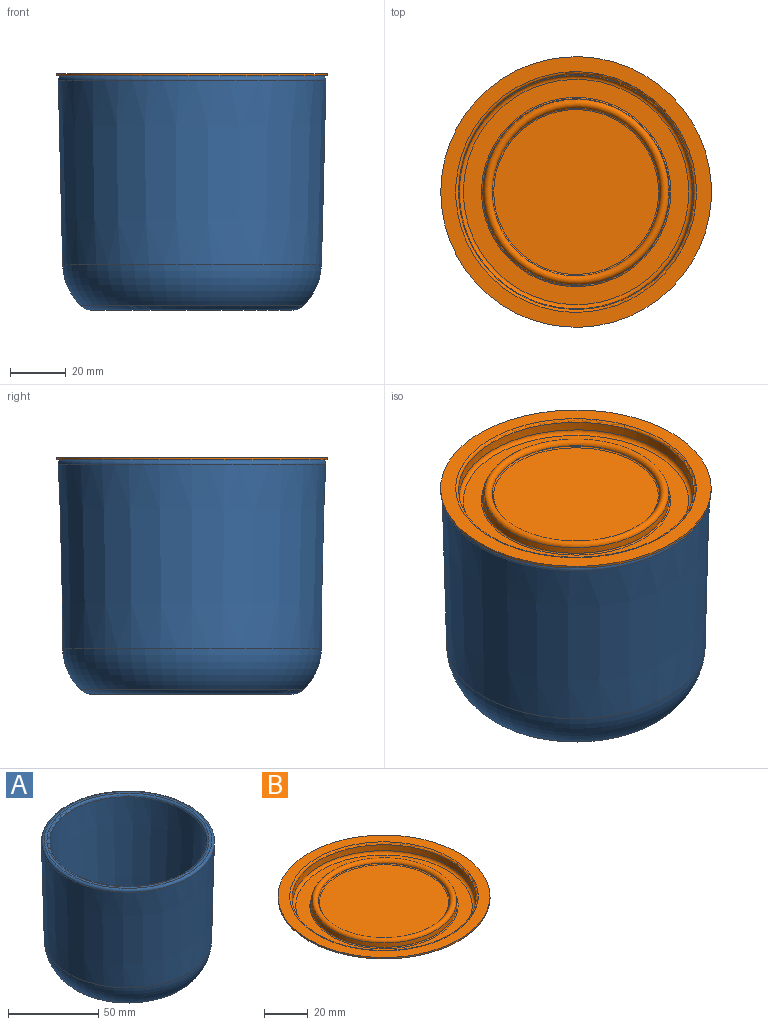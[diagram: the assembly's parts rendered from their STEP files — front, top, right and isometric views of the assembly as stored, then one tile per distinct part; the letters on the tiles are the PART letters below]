
ASSEMBLY  parts=2 mates=1
PART A: 11 faces, bbox 103.8x103.8x88.2 mm
  f0: cone r=43.5mm half-angle=3.5deg, axis (0,0,1), area 18136.1mm2, adj f3,f6
  f1: torus R=35.76mm, axis (0,0,1), area 1107.2mm2, adj f8,f10
  f2: plane 72.35x72.35mm, normal (0,0,1), area 4111.6mm2, adj f3
  f3: torus R=36.18mm, axis (0,0,-1), area 1082.9mm2, adj f0,f2
  f4: torus R=46.46mm, axis (0,0,-1), area 712.8mm2, adj f5,f7
  f5: plane 92.93x92.93mm, normal (0,0,1), area 445.6mm2, adj f4,f6
  f6: torus R=44.91mm, axis (0,0,-1), area 625.9mm2, adj f0,f5
  f7: cone r=46mm half-angle=1.4deg, axis (0,0,1), area 19603.5mm2, adj f4,f9
  f8: cone r=38.2mm half-angle=45.7deg, axis (0,0,1), area 42.3mm2, adj f1,f9
  f9: torus R=25.4mm, axis (0,0,-1), area 4507.6mm2, adj f7,f8
  f10: sphere r=426.91mm, area 4023.6mm2, adj f1
PART B: 23 faces, bbox 97x97x6 mm
  f0: plane 59.27x59.27mm, normal (0,0,-1), area 2758.8mm2, adj f18
  f1: cone r=30.55mm half-angle=5deg, axis (0,0,1), area 33.7mm2, adj f2,f18
  f2: torus R=31.64mm, axis (0,0,-1), area 589.9mm2, adj f1,f3
  f3: cone r=32.64mm half-angle=5deg, axis (0,0,-1), area 490.3mm2, adj f2,f17
  f4: plane 80.92x80.92mm, normal (0,0,-1), area 1545.6mm2, adj f15,f17
  f5: cone r=42.3mm half-angle=5deg, axis (0,0,1), area 783.7mm2, adj f15,f22
  f6: plane 97x97mm, normal (0,0,-1), area 1524.6mm2, adj f7,f22
  f7: cylinder r=48.5mm len=97mm, axis (0,0,-1), area 243.8mm2, adj f6,f8
  f8: plane 97x97mm, normal (0,0,1), area 1544.7mm2, adj f7,f21
  f9: cone r=42.22mm half-angle=5deg, axis (0,0,1), area 826mm2, adj f16,f21
  f10: plane 80.74x80.74mm, normal (0,0,1), area 1502.8mm2, adj f16,f20
  f11: cone r=33.47mm half-angle=5deg, axis (0,0,-1), area 480mm2, adj f12,f20
  f12: torus R=31.64mm, axis (0,0,-1), area 943.8mm2, adj f11,f13
  f13: cone r=30mm half-angle=5deg, axis (0,0,1), area 15.7mm2, adj f12,f19
  f14: plane 59.08x59.08mm, normal (0,0,1), area 2741.7mm2, adj f19
  f15: torus R=40.46mm, axis (0,0,-1), area 777.3mm2, adj f4,f5
  f16: torus R=40.37mm, axis (0,0,1), area 577.4mm2, adj f9,f10
  f17: torus R=33.84mm, axis (0,0,-1), area 309.7mm2, adj f3,f4
  f18: torus R=29.63mm, axis (0,0,-1), area 282mm2, adj f0,f1
  f19: torus R=29.54mm, axis (0,0,-1), area 139.1mm2, adj f13,f14
  f20: torus R=33.93mm, axis (0,0,1), area 156.7mm2, adj f10,f11
  f21: torus R=43.13mm, axis (0,0,1), area 396.3mm2, adj f8,f9
  f22: torus R=43.21mm, axis (0,0,-1), area 199.9mm2, adj f5,f6
PLACE A t=(-7.36,18.17,-8.37)mm
PLACE B t=(-7.36,18.17,70.43)mm
MATE parallel B.f1 <-> A.f0  axis (0,0,-1) through (-7.36,18.17,75.63)mm
